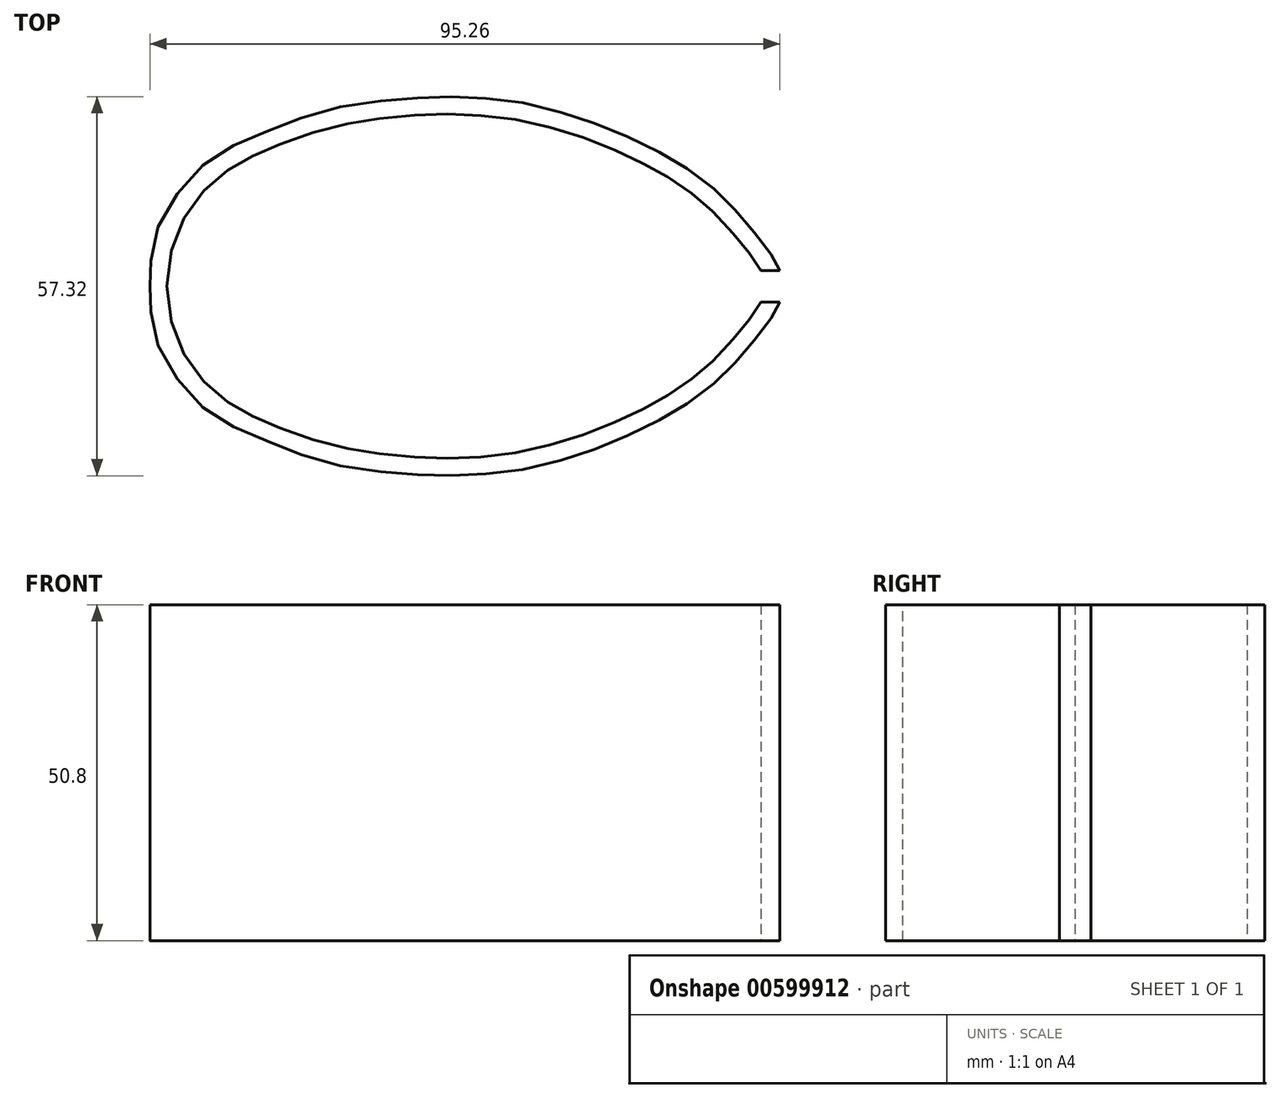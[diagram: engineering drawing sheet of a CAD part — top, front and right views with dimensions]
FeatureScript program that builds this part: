
annotation { "Feature Type Name" : "Feature", "Feature Type Description" : "" }
export const myFeature = defineFeature(function(context is Context, id is Id, definition is map)
    precondition{}
    {
        {
            var Q0;
            Q0=qCreatedBy(makeId("Top.planeOp"),FACE);
            var sketch = newSketch(context, id + "F0", { "sketchPlane" : qUnion([Q0])});
            skPoint(sketch, "E0", {"position": v(-43.82, 0) * mm});
            skSolve(sketch);
        }
        {
            var Q0;
            Q0=qCreatedBy(makeId("Top.planeOp"),FACE);
            var sketch = newSketch(context, id + "F1", { "sketchPlane" : qUnion([Q0])});
            skPoint(sketch, "E1", {"position": v(51.44, 0) * mm});
            skSolve(sketch);
        }
        {
            var Q0;
            Q0=qCreatedBy(makeId("Top.planeOp"),FACE);
            var sketch = newSketch(context, id + "F2", { "sketchPlane" : qUnion([Q0])});
            skPoint(sketch, "E2", {"position": v(0, 28.58) * mm});
            skSolve(sketch);
        }
        {
            var Q0;
            Q0=qCreatedBy(makeId("Top.planeOp"),FACE);
            var sketch = newSketch(context, id + "F3", { "sketchPlane" : qUnion([Q0])});
            skPoint(sketch, "E3", {"position": v(22.07, 0) * mm});
            skSolve(sketch);
        }
        {
            var Q0;
            Q0=qCreatedBy(makeId("Top.planeOp"),FACE);
            var sketch = newSketch(context, id + "F4", { "sketchPlane" : qUnion([Q0])});
            skPoint(sketch, "E4", {"position": v(14.86, 19.05) * mm});
            skSolve(sketch);
        }
        {
            var Q0;
            Q0=qCreatedBy(makeId("Top.planeOp"),FACE);
            var sketch = newSketch(context, id + "F5", { "sketchPlane" : qUnion([Q0])});
            skPoint(sketch, "E5", {"position": v(51.44, 2.39) * mm});
            skSolve(sketch);
        }
        {
            var Q0;
            Q0=qCreatedBy(makeId("Top.planeOp"),FACE);
            var sketch = newSketch(context, id + "F6", { "sketchPlane" : qUnion([Q0])});
            skArc(sketch, "E6", {"start": v(0, 28.58) * mm, "mid": v(-19.2, 25.91) * mm, "end": v(-36.96, 18.13) * mm});
            skSolve(sketch);
        }
        {
            var Q0;
            Q0=qCreatedBy(makeId("Top.planeOp"),FACE);
            var sketch = newSketch(context, id + "F7", { "sketchPlane" : qUnion([Q0])});
            skPoint(sketch, "E7", {"position": v(0, 25.04) * mm});
            skSolve(sketch);
        }
        {
            var Q0;
            Q0=qCreatedBy(makeId("Top.planeOp"),FACE);
            var sketch = newSketch(context, id + "F8", { "sketchPlane" : qUnion([Q0])});
            skLineSegment(sketch, "E8.bottom", {"start": v(46.93, 0) * mm, "end": v(59.21, 0) * mm});
            skLineSegment(sketch, "E8.top", {"start": v(46.93, 2.39) * mm, "end": v(59.21, 2.39) * mm});
            skLineSegment(sketch, "E8.left", {"start": v(46.93, 0) * mm, "end": v(46.93, 2.39) * mm});
            skLineSegment(sketch, "E8.right", {"start": v(59.21, 0) * mm, "end": v(59.21, 2.39) * mm});
            skSolve(sketch);
        }
        {
            var Q0;
            Q0=qCreatedBy(makeId("Top.planeOp"),FACE);
            var sketch = newSketch(context, id + "F9", { "sketchPlane" : qUnion([Q0])});
            skFitSpline(sketch, "E9", {"points": [v(-43.82, 0) * mm, v(-42.29, 8.43) * mm, v(-38.7, 14.76) * mm, v(-33.64, 19.55) * mm, v(-28, 22.56) * mm, v(-21.88, 24.98) * mm, v(-13.72, 27.17) * mm, v(-5.78, 28.23) * mm, v(0, 28.56) * mm, v(5.9, 28.37) * mm, v(12.54, 27.57) * mm, v(19.9, 25.73) * mm, v(25.6, 23.7) * mm, v(31.67, 20.94) * mm, v(36.27, 18.37) * mm, v(40.88, 15.08) * mm, v(44.19, 12) * mm, v(47.1, 8.7) * mm, v(49.61, 5.46) * mm, v(51.44, 2.39) * mm], "startDerivative": vector(2.54, 145.05) * mm, "endDerivative": vector(28.25, -58.97) * mm});
            skSolve(sketch);
        }
        {
            var Q0;
            Q0=qCreatedBy(makeId("Top.planeOp"),FACE);
            var sketch = newSketch(context, id + "F10", { "sketchPlane" : qUnion([Q0])});
            skFitSpline(sketch, "E10.0", {"points": [v(-41.28, 0.01) * mm, v(-41.28, 1.36) * mm, v(-41.03, 4) * mm, v(-40.15, 7.05) * mm, v(-39.2, 9.27) * mm, v(-38.37, 10.83) * mm, v(-37.4, 12.3) * mm, v(-36.33, 13.7) * mm, v(-35.14, 15) * mm, v(-33.86, 16.2) * mm, v(-32.73, 17.1) * mm, v(-31.81, 17.72) * mm, v(-30.86, 18.32) * mm, v(-29.62, 19) * mm, v(-28.3, 19.64) * mm, v(-27.23, 20.13) * mm, v(-26.13, 20.61) * mm, v(-24.77, 21.2) * mm, v(-23.09, 21.86) * mm, v(-21.33, 22.5) * mm, v(-19.46, 23.1) * mm, v(-17.5, 23.69) * mm, v(-15.47, 24.21) * mm, v(-13.76, 24.59) * mm, v(-12.4, 24.84) * mm, v(-11.02, 25.07) * mm, v(-9.32, 25.31) * mm, v(-7.32, 25.54) * mm, v(-5.4, 25.72) * mm, v(-3.63, 25.87) * mm, v(-1.94, 25.97) * mm, v(-0.3, 26.03) * mm, v(1.37, 26.03) * mm, v(3.08, 25.99) * mm, v(4.84, 25.9) * mm, v(6.62, 25.78) * mm, v(8.4, 25.61) * mm, v(10.2, 25.39) * mm, v(12.04, 25.1) * mm, v(13.96, 24.7) * mm, v(15.9, 24.22) * mm, v(17.81, 23.7) * mm, v(19.62, 23.16) * mm, v(21.27, 22.62) * mm, v(22.87, 22.06) * mm, v(24.47, 21.43) * mm, v(26.17, 20.71) * mm, v(27.9, 19.94) * mm, v(29.32, 19.27) * mm, v(30.39, 18.75) * mm, v(31.4, 18.23) * mm, v(32.59, 17.6) * mm, v(33.71, 16.96) * mm, v(34.62, 16.41) * mm, v(35.54, 15.83) * mm, v(36.71, 15.04) * mm, v(37.86, 14.22) * mm, v(38.73, 13.55) * mm, v(39.56, 12.9) * mm, v(40.49, 12.1) * mm, v(41.51, 11.12) * mm, v(42.5, 10.1) * mm, v(43.5, 9) * mm, v(44.33, 8.04) * mm, v(44.98, 7.28) * mm, v(45.61, 6.52) * mm, v(46.2, 5.8) * mm, v(46.77, 5.07) * mm, v(47.18, 4.52) * mm, v(47.57, 3.95) * mm, v(47.96, 3.36) * mm, v(48.33, 2.77) * mm, v(48.67, 2.2) * mm, v(48.95, 1.68) * mm, v(49.09, 1.4) * mm, v(49.14, 1.3) * mm]});
            skSolve(sketch);
        }
        {
            var Q0;
            Q0=qCreatedBy(makeId("Top.planeOp"),FACE);
            var sketch = newSketch(context, id + "F11", { "sketchPlane" : qUnion([Q0])});
            skArc(sketch, "E11", {"start": v(28.78, 19.52) * mm, "mid": v(23.8, 10.32) * mm, "end": v(22.07, 0) * mm});
            skSolve(sketch);
        }
        {
            var Q0;
            Q0=qCreatedBy(makeId("Top.planeOp"),FACE);
            var sketch = newSketch(context, id + "F12", { "sketchPlane" : qUnion([Q0])});
            skArc(sketch, "E12.0", {"start": v(31.12, 18.38) * mm, "mid": v(26.29, 9.75) * mm, "end": v(24.61, 0) * mm});
            skSolve(sketch);
        }
        {
            var Q0;
            Q0=qCreatedBy(makeId("Top.planeOp"),FACE);
            var sketch = newSketch(context, id + "F13", { "sketchPlane" : qUnion([Q0])});
            skLineSegment(sketch, "E13", {"start": v(-11.16, 25.04) * mm, "end": v(12.21, 25.04) * mm});
            skSolve(sketch);
        }
        {
            var Q0;
            Q0=qCreatedBy(makeId("Top.planeOp"),FACE);
            var sketch = newSketch(context, id + "F14", { "sketchPlane" : qUnion([Q0])});
            skLineSegment(sketch, "E14", {"start": v(48.55, 2.39) * mm, "end": v(51.44, 2.39) * mm});
            skSolve(sketch);
        }
        {
            var Q0;
            Q0=qCreatedBy(makeId("Top.planeOp"),FACE);
            var sketch = newSketch(context, id + "F15", { "sketchPlane" : qUnion([Q0])});
            skLineSegment(sketch, "E15", {"start": v(-43.82, 0) * mm, "end": v(-41.27, 0) * mm});
            skSolve(sketch);
        }
        {
            var Q0;
            Q0=qCreatedBy(makeId("Top.planeOp"),FACE);
            var sketch = newSketch(context, id + "F16", { "sketchPlane" : qUnion([Q0])});
            skLineSegment(sketch, "E16", {"start": v(24.61, 0) * mm, "end": v(22.07, 0) * mm});
            skSolve(sketch);
        }
        {
            var Q0;
            Q0=qCreatedBy(makeId("Top.planeOp"),FACE);
            var sketch = newSketch(context, id + "F17", { "sketchPlane" : qUnion([Q0])});
            skLineSegment(sketch, "E17", {"start": v(-41.27, 0) * mm, "end": v(-41.27, 0.01) * mm});
            skSolve(sketch);
        }
        {
            var Q0;
            Q0=qCreatedBy(makeId("Top.planeOp"),FACE);
            var sketch = newSketch(context, id + "F18", { "sketchPlane" : qUnion([Q0])});
            skLineSegment(sketch, "E18.0", {"start": v(-41.27, 0) * mm, "end": v(-41.27, 0.01) * mm});
            skLineSegment(sketch, "E19.0", {"start": v(-43.82, 0) * mm, "end": v(-41.27, 0) * mm});
            skFitSpline(sketch, "E20.0", {"points": [v(-43.82, 0) * mm, v(-43.76, 3) * mm, v(-42.74, 8.52) * mm, v(-39, 14.92) * mm, v(-33.86, 19.83) * mm, v(-27.97, 22.64) * mm, v(-21.87, 25.13) * mm, v(-13.8, 27.4) * mm, v(-5.87, 28.28) * mm, v(-0.05, 28.66) * mm, v(6, 28.43) * mm, v(12.54, 27.76) * mm, v(19.96, 25.8) * mm, v(25.53, 23.83) * mm, v(31.74, 21) * mm, v(36.24, 18.5) * mm, v(40.96, 15.18) * mm, v(44.2, 12.1) * mm, v(47.12, 8.7) * mm, v(49.6, 5.66) * mm, v(51.06, 3.18) * mm, v(51.44, 2.39) * mm]});
            skFitSpline(sketch, "E21.0", {"points": [v(-41.28, -0.04) * mm, v(-41.25, 1.33) * mm, v(-41.05, 3.34) * mm, v(-40.48, 5.85) * mm, v(-39.91, 7.62) * mm, v(-39.2, 9.27) * mm, v(-38.37, 10.82) * mm, v(-37.41, 12.3) * mm, v(-36.33, 13.7) * mm, v(-35.13, 15) * mm, v(-33.85, 16.2) * mm, v(-32.73, 17.1) * mm, v(-31.81, 17.72) * mm, v(-30.86, 18.32) * mm, v(-29.62, 19) * mm, v(-28.3, 19.64) * mm, v(-27.23, 20.13) * mm, v(-26.13, 20.61) * mm, v(-24.76, 21.2) * mm, v(-23.09, 21.86) * mm, v(-21.33, 22.5) * mm, v(-19.46, 23.1) * mm, v(-17.5, 23.69) * mm, v(-15.47, 24.21) * mm, v(-13.76, 24.59) * mm, v(-12.4, 24.84) * mm, v(-11.02, 25.07) * mm, v(-9.32, 25.31) * mm, v(-7.32, 25.54) * mm, v(-5.4, 25.72) * mm, v(-3.63, 25.87) * mm, v(-1.94, 25.97) * mm, v(-0.3, 26.03) * mm, v(1.37, 26.03) * mm, v(3.08, 25.99) * mm, v(4.84, 25.9) * mm, v(6.62, 25.78) * mm, v(8.4, 25.61) * mm, v(10.2, 25.39) * mm, v(12.04, 25.1) * mm, v(13.96, 24.7) * mm, v(15.9, 24.22) * mm, v(17.81, 23.7) * mm, v(19.62, 23.16) * mm, v(21.27, 22.62) * mm, v(22.87, 22.06) * mm, v(24.47, 21.43) * mm, v(26.17, 20.71) * mm, v(27.9, 19.94) * mm, v(29.32, 19.27) * mm, v(30.39, 18.75) * mm, v(31.4, 18.23) * mm, v(32.59, 17.6) * mm, v(33.71, 16.96) * mm, v(34.62, 16.41) * mm, v(35.54, 15.83) * mm, v(36.71, 15.04) * mm, v(37.86, 14.22) * mm, v(38.73, 13.55) * mm, v(39.56, 12.9) * mm, v(40.49, 12.1) * mm, v(41.51, 11.12) * mm, v(42.5, 10.1) * mm, v(43.5, 9) * mm, v(44.33, 8.04) * mm, v(44.98, 7.28) * mm, v(45.61, 6.52) * mm, v(46.2, 5.8) * mm, v(46.77, 5.07) * mm, v(47.18, 4.52) * mm, v(47.57, 3.95) * mm, v(47.96, 3.36) * mm, v(48.33, 2.77) * mm, v(48.67, 2.2) * mm, v(48.95, 1.68) * mm, v(49.09, 1.4) * mm, v(49.14, 1.3) * mm]});
            skLineSegment(sketch, "E22.0", {"start": v(-11.16, 25.04) * mm, "end": v(12.21, 25.04) * mm});
            skArc(sketch, "E23.0", {"start": v(28.78, 19.52) * mm, "mid": v(23.8, 10.32) * mm, "end": v(22.07, 0) * mm});
            skArc(sketch, "E24.0", {"start": v(31.12, 18.38) * mm, "mid": v(26.29, 9.75) * mm, "end": v(24.61, 0) * mm});
            skLineSegment(sketch, "E25.0", {"start": v(24.61, 0) * mm, "end": v(22.07, 0) * mm});
            skLineSegment(sketch, "E26.0", {"start": v(48.55, 2.39) * mm, "end": v(51.44, 2.39) * mm});
            skSolve(sketch);
        }
        {
            var Q0;
            Q0=qSketchRegion(id+"F18",true);
            extrude(context, id + "F19", {"entities" : qUnion([Q0]), "depth" : 50.8 * mm, "offsetDistance" : 25.4 * mm, "symmetric" : true});
        }
        {
            var Q0;
            Q0=makeQuery(id+"F19.opExtrude","SWEPT_BODY",BODY,{"disambiguationData":[OSD([sQuery(id+"F18.wireOp",EDGE,"E18.0"),sQuery(id+"F18.wireOp",EDGE,"E19.0"),sQuery(id+"F18.wireOp",EDGE,"E20.0"),sQuery(id+"F18.wireOp",EDGE,"E21.0"),sQuery(id+"F18.wireOp",EDGE,"E22.0"),sQuery(id+"F18.wireOp",EDGE,"E23.0"),sQuery(id+"F18.wireOp",EDGE,"E24.0"),sQuery(id+"F18.wireOp",EDGE,"E25.0"),sQuery(id+"F18.wireOp",EDGE,"E26.0")])]});
            var Q1;
            Q1=qCreatedBy(makeId("Front.planeOp"),FACE);
            mirror(context, id + "F20", {"operationType" : NewBodyOperationType.ADD, "entities" : qUnion([Q0]), "mirrorPlane" : qUnion([Q1])});
        }
    });
